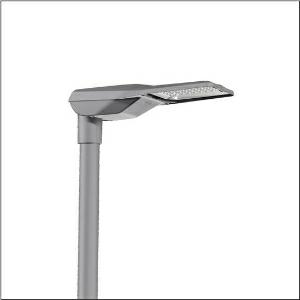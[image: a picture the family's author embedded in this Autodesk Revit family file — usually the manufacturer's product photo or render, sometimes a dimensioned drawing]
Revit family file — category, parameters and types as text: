
# Revit family: streetlight_sl_21_iq_mini___st1_0ab_5xe2m31d08jb_643a
name_source: partatom
category: Lighting Fixtures
units: mm (PartAtom-declared; Revit-internal decimal feet)

## family parameters
Cut with Voids When Loaded = No
Host = Face
Light Source = No
Part Type = Normal
Room Calculation Point = No
Round Connector Dimension = Use Diameter
Shared = No

## types (1)
- --- (1 x LED, 9530 lm, 71.6 W, 3000K)
    Apparent Load = 72 VA
    CIE Flux Codes = 40 74 97 100 100
    Color Rendering = 70
    Color Temperature = 3000K
    Default Elevation = 1800 mm
    Description = Streetlight SL 21 iQ mini, mast luminaire, primary light control with lens, of PMMA, primary optical cover: cover, of toughened safety glass, transparent, light distribution: ST1.0aB, light emission: direct distribution, primary light characteristic: asymmetric, installation type: post-top, side-entry, LED, High Power LED, rated luminous flux: 9.530lm, luminous efficacy: 133lm/W, light colour: 730, colour temperature: 3000K, control gear: iQ-Comfort, control: Auto-Match, Temp-Guard, Lumen-Switch, Night-Set, Smart-Wire, Light-Fading, Desk-Remote (wireless, voltage-free reading and setting of iQ features in the workshop via application-optimized NFC function/RFID function), optimised constant luminous flux control (CLO 2.0), pre-setting: linear dimming characteristic, mains connection: 220..240V, AC, 50/60Hz, start of lifetime: 72W, end of service life: 75W, reduction: 33W, luminaire housing, of diecast aluminium, powder-coated, Siteco® metallic grey (DB 702S), corrosivity category C5 mid according to DIN EN ISO 12944, please order mast flange separately, inclination adjustable: 0°, 5°, 10°, 15°, sealing non-destructively replaceable, multi-level sealing system, length: 628mm, width: 235mm, height: 110mm, mast flange for spigot size: 42mm (side-entry): 5XC10008XM4, 60/48mm (side-entry/post-top): 5XC10108XM2, 76/60mm (side-entry/post-top): 5XC10108XM1, mounting height: 4..8m, protection rating (complete): IP66, insulation class (complete): insulation class II (safety insulation), certification: CE, ENEC, ENEC+, VDE, impact resistance: IK10, permissible operating ambient temperature for outdoor applications: -40..+50°C, standard-compliant lighting for roads and squares, packaging unit: 1 piece

Light Distribution: ST1.0aB
    Height = 110 mm
    Lamp = 1 x LED
    Lamp Light Flux = 9530 lm
    Lamp Power = 71.6 W
    Lamp count = 1
    Length = 625 mm
    Luminous efficacy = 133 lm/W
    Manufacturer = Siteco
    ModVariant = No
    Model = 5XE2M31D08JB
    Number of Poles = 1
    OnlyDefault = Yes
    Power Factor = 1
    Product Name = Streetlight SL 21 iQ mini | ST1.0aB
    Product group = mast luminaire | pylon top
    ProductGroupID = 6100
    Protection Class = Protection class II
    Protection Degree = IP 66
    RLX_Detail_Level = 1
    RLX_Emergency_Light_Flux = 0 lm
    RLX_Emergency_Type = 0
    RLX_Emergency_Type_DB = No
    RlxData = <blob elided: 26341 chars, md5=dd81ddb6>
    Socket = socket
    Standby Power = 0 W
    System Light Flux = 9530 lm
    System Power = 72 W
    Type Comments = factory setting: luminous flux: 100 % | dim-lin: 254 | 746 mA
    Type Image = l_1003519.jpg
    URL = http://relux.com
    VarID = @adj_168378
    Voltage = 0 V
    Weight = 0.00 kg
    Width = 234 mm

## geometry (parser evidence)
native form markers: Blend x4, Sweep x12
no freeform markers — native parametric forms only
